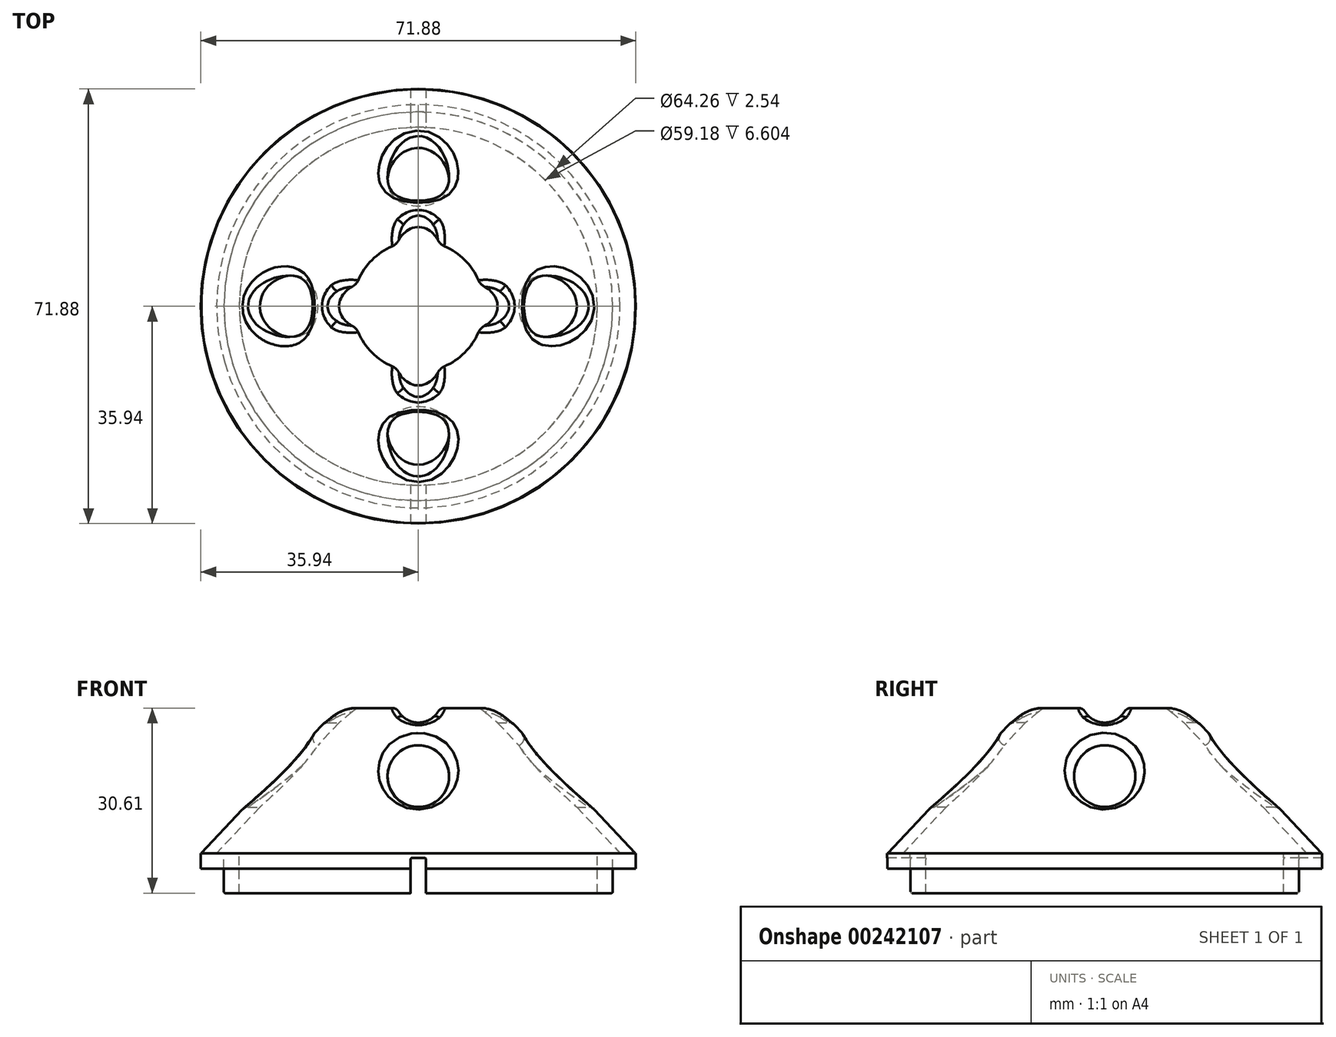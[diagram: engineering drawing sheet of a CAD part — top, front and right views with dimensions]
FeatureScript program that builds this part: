
annotation { "Feature Type Name" : "Feature", "Feature Type Description" : "" }
export const myFeature = defineFeature(function(context is Context, id is Id, definition is map)
    precondition{}
    {
        {
            var Q0;
            Q0=qCreatedBy(makeId("Top.planeOp"),FACE);
            var sketch = newSketch(context, id + "F0", { "sketchPlane" : qUnion([Q0])});
            skCircle(sketch, "E0", {"center": v(0, 0) * mm, "radius": 32.13 * mm});
            skCircle(sketch, "E1", {"center": v(0, 0) * mm, "radius": 35.94 * mm});
            skCircle(sketch, "E2", {"center": v(0, 0) * mm, "radius": 29.6 * mm});
            skSolve(sketch);
        }
        {
            var Q0;
            Q0=makeQuery(id+"F0.imprint","IMPRINT",FACE,{"disambiguationData":[TD([[makeQuery(id+"F0.imprint","IMPRINT",EDGE,{"derivedFrom":sQuery(id+"F0.wireOp",EDGE,"E0")}),1.0]])]});
            extrude(context, id + "F1", {"entities" : qUnion([Q0]), "oppositeDirection" : true, "depth" : 6.6 * mm});
        }
        {
            var Q0;
            Q0=makeQuery(id+"F0.imprint","IMPRINT",FACE,{"disambiguationData":[TD([[makeQuery(id+"F0.imprint","IMPRINT",EDGE,{"derivedFrom":sQuery(id+"F0.wireOp",EDGE,"E0")}),-1.0]])]});
            extrude(context, id + "F2", {"entities" : qUnion([Q0]), "oppositeDirection" : true, "depth" : 2.54 * mm});
        }
        {
            var Q0;
            Q0=qCreatedBy(makeId("Front.planeOp"),FACE);
            var sketch = newSketch(context, id + "F3", { "sketchPlane" : qUnion([Q0])});
            skPoint(sketch, "E3", {"position": v(-35.87, 0) * mm});
            skPoint(sketch, "E4", {"position": v(-33.33, 0) * mm});
            skPoint(sketch, "E5", {"position": v(0, 38.1) * mm});
            skPoint(sketch, "E6", {"position": v(0, 35.56) * mm});
            skLineSegment(sketch, "E7", {"start": v(0, 38.1) * mm, "end": v(-35.87, 0) * mm});
            skLineSegment(sketch, "E8", {"start": v(0, 35.56) * mm, "end": v(-33.33, 0) * mm});
            skLineSegment(sketch, "E9", {"start": v(0, 38.1) * mm, "end": v(0, 35.56) * mm});
            skLineSegment(sketch, "E10", {"start": v(-35.87, 0) * mm, "end": v(-33.33, 0) * mm});
            skSolve(sketch);
        }
        {
            var Q0;
            Q0=makeQuery(id+"F3.imprint","IMPRINT",FACE,{"disambiguationData":[TD([[makeQuery(id+"F3.imprint","IMPRINT",EDGE,{"derivedFrom":sQuery(id+"F3.wireOp",EDGE,"E7")}),1.0]])]});
            var Q1;
            Q1=sQuery(id+"F3.wireOp",EDGE,"E9");
            revolve(context, id + "F4", {"entities" : qUnion([Q0]), "axis" : qUnion([Q1]), "revolveType" : RevolveType.FULL});
        }
        {
            var Q0;
            Q0=qCreatedBy(makeId("Front.planeOp"),FACE);
            var sketch = newSketch(context, id + "F5", { "sketchPlane" : qUnion([Q0])});
            skPoint(sketch, "E11", {"position": v(0, 25.4) * mm});
            skCircle(sketch, "E12", {"center": v(0, 25.4) * mm, "radius": 3.81 * mm});
            skPoint(sketch, "E13", {"position": v(0, 12.7) * mm});
            skCircle(sketch, "E14", {"center": v(0, 12.7) * mm, "radius": 5.08 * mm});
            skSolve(sketch);
        }
        {
            var Q0;
            Q0 = qSketchRegion(id + "F5", true);
            extrude(context, id + "F6", {"entities" : qUnion([Q0]), "operationType" : NewBodyOperationType.REMOVE, "endBound" : BoundingType.SYMMETRIC, "oppositeDirection" : true, "depth" : 76.2 * mm});
        }
        {
            var Q0;
            Q0=qCreatedBy(makeId("Right.planeOp"),FACE);
            var sketch = newSketch(context, id + "F7", { "sketchPlane" : qUnion([Q0])});
            skPoint(sketch, "E15", {"position": v(0, 25.4) * mm});
            skCircle(sketch, "E16", {"center": v(0, 25.4) * mm, "radius": 3.81 * mm});
            skCircle(sketch, "E17", {"center": v(0, 12.7) * mm, "radius": 5.08 * mm});
            skSolve(sketch);
        }
        {
            var Q0;
            Q0 = qSketchRegion(id + "F7", true);
            extrude(context, id + "F8", {"entities" : qUnion([Q0]), "operationType" : NewBodyOperationType.REMOVE, "endBound" : BoundingType.SYMMETRIC, "oppositeDirection" : true, "depth" : 76.2 * mm});
        }
        {
            var Q0;
            Q0=qCreatedBy(makeId("Front.planeOp"),FACE);
            var sketch = newSketch(context, id + "F9", { "sketchPlane" : qUnion([Q0])});
            skLineSegment(sketch, "E18.bottom", {"start": v(1.27, -0.77) * mm, "end": v(-1.27, -0.77) * mm});
            skLineSegment(sketch, "E18.top", {"start": v(1.27, -14.3) * mm, "end": v(-1.27, -14.3) * mm});
            skLineSegment(sketch, "E18.left", {"start": v(1.27, -0.77) * mm, "end": v(1.27, -14.3) * mm});
            skLineSegment(sketch, "E18.right", {"start": v(-1.27, -0.77) * mm, "end": v(-1.27, -14.3) * mm});
            skPoint(sketch, "E18.middle", {"position": v(0, -7.54) * mm});
            skSolve(sketch);
        }
        {
            var Q0;
            Q0 = qSketchRegion(id + "F9", true);
            extrude(context, id + "F10", {"entities" : qUnion([Q0]), "operationType" : NewBodyOperationType.REMOVE, "endBound" : BoundingType.SYMMETRIC, "oppositeDirection" : true, "depth" : 127 * mm});
        }
        {
            var Q0;
            {var subQ0=sQuery(id+"F9.wireOp",EDGE,"E18.bottom");var subQ1=sQuery(id+"F9.wireOp",EDGE,"E18.left");Q0=makeQuery(id+"F10.boolean.opBoolean","COPY",EDGE,{"disambiguationData":[TD([makeQuery(id+"F2.opExtrude","SWEPT_FACE",FACE,{"disambiguationData":[OSD([sQuery(id+"F0.wireOp",EDGE,"E0")])]}),makeQuery(id+"F2.opExtrude","SWEPT_FACE",FACE,{"disambiguationData":[OSD([sQuery(id+"F0.wireOp",EDGE,"E1")])]}),makeQuery(id+"F10.opExtrude","SWEPT_FACE",FACE,{"disambiguationData":[OSD([subQ0])]}),makeQuery(id+"F10.opExtrude","SWEPT_FACE",FACE,{"disambiguationData":[OSD([subQ1])]})]),OD(0.0)],"derivedFrom":makeQuery(id+"F10.opExtrude","SWEPT_EDGE",EDGE,{"disambiguationData":[OSD([subQ0,subQ1])]})});}
            var Q1;
            {var subQ0=sQuery(id+"F9.wireOp",EDGE,"E18.left");var subQ1=sQuery(id+"F9.wireOp",EDGE,"E18.bottom");Q1=makeQuery(id+"F10.boolean.opBoolean","COPY",EDGE,{"disambiguationData":[TD([makeQuery(id+"F1.opExtrude","SWEPT_FACE",FACE,{"disambiguationData":[OSD([sQuery(id+"F0.wireOp",EDGE,"E0")])]}),makeQuery(id+"F1.opExtrude","SWEPT_FACE",FACE,{"disambiguationData":[OSD([sQuery(id+"F0.wireOp",EDGE,"E2")])]}),makeQuery(id+"F10.opExtrude","SWEPT_FACE",FACE,{"disambiguationData":[OSD([subQ1])]}),makeQuery(id+"F10.opExtrude","SWEPT_FACE",FACE,{"disambiguationData":[OSD([subQ0])]})]),OD(0.0)],"derivedFrom":makeQuery(id+"F10.opExtrude","SWEPT_EDGE",EDGE,{"disambiguationData":[OSD([subQ1,subQ0])]})});}
            var Q2;
            {var subQ0=sQuery(id+"F9.wireOp",EDGE,"E18.bottom");var subQ1=sQuery(id+"F9.wireOp",EDGE,"E18.right");Q2=makeQuery(id+"F10.boolean.opBoolean","COPY",EDGE,{"disambiguationData":[TD([makeQuery(id+"F1.opExtrude","SWEPT_FACE",FACE,{"disambiguationData":[OSD([sQuery(id+"F0.wireOp",EDGE,"E0")])]}),makeQuery(id+"F1.opExtrude","SWEPT_FACE",FACE,{"disambiguationData":[OSD([sQuery(id+"F0.wireOp",EDGE,"E2")])]}),makeQuery(id+"F10.opExtrude","SWEPT_FACE",FACE,{"disambiguationData":[OSD([subQ0])]}),makeQuery(id+"F10.opExtrude","SWEPT_FACE",FACE,{"disambiguationData":[OSD([subQ1])]})]),OD(0.0)],"derivedFrom":makeQuery(id+"F10.opExtrude","SWEPT_EDGE",EDGE,{"disambiguationData":[OSD([subQ0,subQ1])]})});}
            var Q3;
            {var subQ0=sQuery(id+"F9.wireOp",EDGE,"E18.bottom");var subQ1=sQuery(id+"F9.wireOp",EDGE,"E18.right");Q3=makeQuery(id+"F10.boolean.opBoolean","COPY",EDGE,{"disambiguationData":[TD([makeQuery(id+"F2.opExtrude","SWEPT_FACE",FACE,{"disambiguationData":[OSD([sQuery(id+"F0.wireOp",EDGE,"E0")])]}),makeQuery(id+"F2.opExtrude","SWEPT_FACE",FACE,{"disambiguationData":[OSD([sQuery(id+"F0.wireOp",EDGE,"E1")])]}),makeQuery(id+"F10.opExtrude","SWEPT_FACE",FACE,{"disambiguationData":[OSD([subQ0])]}),makeQuery(id+"F10.opExtrude","SWEPT_FACE",FACE,{"disambiguationData":[OSD([subQ1])]})]),OD(0.0)],"derivedFrom":makeQuery(id+"F10.opExtrude","SWEPT_EDGE",EDGE,{"disambiguationData":[OSD([subQ0,subQ1])]})});}
            var Q4;
            {var subQ0=sQuery(id+"F9.wireOp",EDGE,"E18.bottom");var subQ1=sQuery(id+"F9.wireOp",EDGE,"E18.right");Q4=makeQuery(id+"F10.boolean.opBoolean","COPY",EDGE,{"disambiguationData":[TD([makeQuery(id+"F2.opExtrude","SWEPT_FACE",FACE,{"disambiguationData":[OSD([sQuery(id+"F0.wireOp",EDGE,"E0")])]}),makeQuery(id+"F2.opExtrude","SWEPT_FACE",FACE,{"disambiguationData":[OSD([sQuery(id+"F0.wireOp",EDGE,"E1")])]}),makeQuery(id+"F10.opExtrude","SWEPT_FACE",FACE,{"disambiguationData":[OSD([subQ0])]}),makeQuery(id+"F10.opExtrude","SWEPT_FACE",FACE,{"disambiguationData":[OSD([subQ1])]})]),OD(1.0)],"derivedFrom":makeQuery(id+"F10.opExtrude","SWEPT_EDGE",EDGE,{"disambiguationData":[OSD([subQ0,subQ1])]})});}
            var Q5;
            {var subQ0=sQuery(id+"F9.wireOp",EDGE,"E18.bottom");var subQ1=sQuery(id+"F9.wireOp",EDGE,"E18.right");Q5=makeQuery(id+"F10.boolean.opBoolean","COPY",EDGE,{"disambiguationData":[TD([makeQuery(id+"F1.opExtrude","SWEPT_FACE",FACE,{"disambiguationData":[OSD([sQuery(id+"F0.wireOp",EDGE,"E0")])]}),makeQuery(id+"F1.opExtrude","SWEPT_FACE",FACE,{"disambiguationData":[OSD([sQuery(id+"F0.wireOp",EDGE,"E2")])]}),makeQuery(id+"F10.opExtrude","SWEPT_FACE",FACE,{"disambiguationData":[OSD([subQ0])]}),makeQuery(id+"F10.opExtrude","SWEPT_FACE",FACE,{"disambiguationData":[OSD([subQ1])]})]),OD(1.0)],"derivedFrom":makeQuery(id+"F10.opExtrude","SWEPT_EDGE",EDGE,{"disambiguationData":[OSD([subQ0,subQ1])]})});}
            var Q6;
            {var subQ0=sQuery(id+"F9.wireOp",EDGE,"E18.bottom");var subQ1=sQuery(id+"F9.wireOp",EDGE,"E18.left");Q6=makeQuery(id+"F10.boolean.opBoolean","COPY",EDGE,{"disambiguationData":[TD([makeQuery(id+"F2.opExtrude","SWEPT_FACE",FACE,{"disambiguationData":[OSD([sQuery(id+"F0.wireOp",EDGE,"E0")])]}),makeQuery(id+"F2.opExtrude","SWEPT_FACE",FACE,{"disambiguationData":[OSD([sQuery(id+"F0.wireOp",EDGE,"E1")])]}),makeQuery(id+"F10.opExtrude","SWEPT_FACE",FACE,{"disambiguationData":[OSD([subQ0])]}),makeQuery(id+"F10.opExtrude","SWEPT_FACE",FACE,{"disambiguationData":[OSD([subQ1])]})]),OD(1.0)],"derivedFrom":makeQuery(id+"F10.opExtrude","SWEPT_EDGE",EDGE,{"disambiguationData":[OSD([subQ0,subQ1])]})});}
            var Q7;
            {var subQ0=sQuery(id+"F9.wireOp",EDGE,"E18.left");var subQ1=sQuery(id+"F9.wireOp",EDGE,"E18.bottom");Q7=makeQuery(id+"F10.boolean.opBoolean","COPY",EDGE,{"disambiguationData":[TD([makeQuery(id+"F1.opExtrude","SWEPT_FACE",FACE,{"disambiguationData":[OSD([sQuery(id+"F0.wireOp",EDGE,"E0")])]}),makeQuery(id+"F1.opExtrude","SWEPT_FACE",FACE,{"disambiguationData":[OSD([sQuery(id+"F0.wireOp",EDGE,"E2")])]}),makeQuery(id+"F10.opExtrude","SWEPT_FACE",FACE,{"disambiguationData":[OSD([subQ1])]}),makeQuery(id+"F10.opExtrude","SWEPT_FACE",FACE,{"disambiguationData":[OSD([subQ0])]})]),OD(1.0)],"derivedFrom":makeQuery(id+"F10.opExtrude","SWEPT_EDGE",EDGE,{"disambiguationData":[OSD([subQ1,subQ0])]})});}
            var Q8;
            {var subQ0=sQuery(id+"F0.wireOp",EDGE,"E0");Q8=makeQuery(id+"F10.boolean.opBoolean","SPLIT",EDGE,{"disambiguationData":[TD([makeQuery(id+"F10.opExtrude","SWEPT_FACE",FACE,{"disambiguationData":[OSD([sQuery(id+"F9.wireOp",EDGE,"E18.right")])]})])],"derivedFrom":makeQuery(id+"F1.opExtrude","CAP_EDGE",EDGE,{"disambiguationData":[OSD([subQ0])],"isStart":false})});}
            var Q9;
            {var subQ0=sQuery(id+"F0.wireOp",EDGE,"E0");Q9=makeQuery(id+"F10.boolean.opBoolean","SPLIT",EDGE,{"disambiguationData":[TD([makeQuery(id+"F10.opExtrude","SWEPT_FACE",FACE,{"disambiguationData":[OSD([sQuery(id+"F9.wireOp",EDGE,"E18.left")])]})])],"derivedFrom":makeQuery(id+"F1.opExtrude","CAP_EDGE",EDGE,{"disambiguationData":[OSD([subQ0])],"isStart":false})});}
            fillet(context, id + "F11", {"entities" : qUnion([Q0, Q1, Q2, Q3, Q4, Q5, Q6, Q7, Q8, Q9]), "radius" : 0.25 * mm, "tangentPropagation" : true, "allowEdgeOverflow" : false});
        }
        {
            var Q0;
            Q0=qCreatedBy(makeId("Top.planeOp"),FACE);
            var sketch = newSketch(context, id + "F12", { "sketchPlane" : qUnion([Q0])});
            skCircle(sketch, "E19", {"center": v(0, 0) * mm, "radius": 10.83 * mm});
            skSolve(sketch);
        }
        {
            var Q0;
            Q0 = qSketchRegion(id + "F12", true);
            extrude(context, id + "F13", {"entities" : qUnion([Q0]), "operationType" : NewBodyOperationType.REMOVE, "depth" : 50.8 * mm});
        }
        {
            var Q0;
            Q0=makeQuery(id+"F13.boolean.opBoolean","INTERSECT",EDGE,{"disambiguationData":[OD(2.0)],"derivedFrom":[makeQuery(id+"F4.opRevolve","SWEPT_FACE",FACE,{"disambiguationData":[OSD([sQuery(id+"F3.wireOp",EDGE,"E7")])]}),makeQuery(id+"F13.opExtrude","SWEPT_FACE",FACE,{"disambiguationData":[OSD([sQuery(id+"F12.wireOp",EDGE,"E19")])]})]});
            var Q1;
            Q1=makeQuery(id+"F13.boolean.opBoolean","INTERSECT",EDGE,{"disambiguationData":[OD(1.0)],"derivedFrom":[makeQuery(id+"F4.opRevolve","SWEPT_FACE",FACE,{"disambiguationData":[OSD([sQuery(id+"F3.wireOp",EDGE,"E7")])]}),makeQuery(id+"F13.opExtrude","SWEPT_FACE",FACE,{"disambiguationData":[OSD([sQuery(id+"F12.wireOp",EDGE,"E19")])]})]});
            var Q2;
            Q2=makeQuery(id+"F13.boolean.opBoolean","INTERSECT",EDGE,{"disambiguationData":[OD(0.0)],"derivedFrom":[makeQuery(id+"F4.opRevolve","SWEPT_FACE",FACE,{"disambiguationData":[OSD([sQuery(id+"F3.wireOp",EDGE,"E7")])]}),makeQuery(id+"F13.opExtrude","SWEPT_FACE",FACE,{"disambiguationData":[OSD([sQuery(id+"F12.wireOp",EDGE,"E19")])]})]});
            var Q3;
            Q3=makeQuery(id+"F13.boolean.opBoolean","INTERSECT",EDGE,{"disambiguationData":[OD(3.0)],"derivedFrom":[makeQuery(id+"F4.opRevolve","SWEPT_FACE",FACE,{"disambiguationData":[OSD([sQuery(id+"F3.wireOp",EDGE,"E7")])]}),makeQuery(id+"F13.opExtrude","SWEPT_FACE",FACE,{"disambiguationData":[OSD([sQuery(id+"F12.wireOp",EDGE,"E19")])]})]});
            fillet(context, id + "F14", {"entities" : qUnion([Q0, Q1, Q2, Q3]), "radius" : 5.08 * mm, "tangentPropagation" : true, "allowEdgeOverflow" : false});
        }
        {
            var Q0;
            Q0=makeQuery(id+"F8.boolean.opBoolean","INTERSECT",EDGE,{"disambiguationData":[OD(0.0)],"derivedFrom":[makeQuery(id+"F4.opRevolve","SWEPT_FACE",FACE,{"disambiguationData":[OSD([sQuery(id+"F3.wireOp",EDGE,"E7")])]}),makeQuery(id+"F8.opExtrude","SWEPT_FACE",FACE,{"disambiguationData":[OSD([sQuery(id+"F7.wireOp",EDGE,"E17")])]})]});
            var Q1;
            Q1=makeQuery(id+"F8.boolean.opBoolean","INTERSECT",EDGE,{"disambiguationData":[OD(1.0)],"derivedFrom":[makeQuery(id+"F4.opRevolve","SWEPT_FACE",FACE,{"disambiguationData":[OSD([sQuery(id+"F3.wireOp",EDGE,"E7")])]}),makeQuery(id+"F8.opExtrude","SWEPT_FACE",FACE,{"disambiguationData":[OSD([sQuery(id+"F7.wireOp",EDGE,"E17")])]})]});
            var Q2;
            Q2=makeQuery(id+"F6.boolean.opBoolean","INTERSECT",EDGE,{"disambiguationData":[OD(1.0)],"derivedFrom":[makeQuery(id+"F4.opRevolve","SWEPT_FACE",FACE,{"disambiguationData":[OSD([sQuery(id+"F3.wireOp",EDGE,"E7")])]}),makeQuery(id+"F6.opExtrude","SWEPT_FACE",FACE,{"disambiguationData":[OSD([sQuery(id+"F5.wireOp",EDGE,"E14")])]})]});
            var Q3;
            Q3=makeQuery(id+"F6.boolean.opBoolean","INTERSECT",EDGE,{"disambiguationData":[OD(0.0)],"derivedFrom":[makeQuery(id+"F4.opRevolve","SWEPT_FACE",FACE,{"disambiguationData":[OSD([sQuery(id+"F3.wireOp",EDGE,"E7")])]}),makeQuery(id+"F6.opExtrude","SWEPT_FACE",FACE,{"disambiguationData":[OSD([sQuery(id+"F5.wireOp",EDGE,"E14")])]})]});
            var Q4;
            Q4=makeQuery(id+"F8.boolean.opBoolean","INTERSECT",EDGE,{"disambiguationData":[OD(1.0)],"derivedFrom":[makeQuery(id+"F4.opRevolve","SWEPT_FACE",FACE,{"disambiguationData":[OSD([sQuery(id+"F3.wireOp",EDGE,"E7")])]}),makeQuery(id+"F8.opExtrude","SWEPT_FACE",FACE,{"disambiguationData":[OSD([sQuery(id+"F7.wireOp",EDGE,"E16")])]})]});
            var Q5;
            Q5=makeQuery(id+"F6.boolean.opBoolean","INTERSECT",EDGE,{"disambiguationData":[OD(1.0)],"derivedFrom":[makeQuery(id+"F4.opRevolve","SWEPT_FACE",FACE,{"disambiguationData":[OSD([sQuery(id+"F3.wireOp",EDGE,"E7")])]}),makeQuery(id+"F6.opExtrude","SWEPT_FACE",FACE,{"disambiguationData":[OSD([sQuery(id+"F5.wireOp",EDGE,"E12")])]})]});
            var Q6;
            Q6=makeQuery(id+"F8.boolean.opBoolean","INTERSECT",EDGE,{"disambiguationData":[OD(0.0)],"derivedFrom":[makeQuery(id+"F4.opRevolve","SWEPT_FACE",FACE,{"disambiguationData":[OSD([sQuery(id+"F3.wireOp",EDGE,"E7")])]}),makeQuery(id+"F8.opExtrude","SWEPT_FACE",FACE,{"disambiguationData":[OSD([sQuery(id+"F7.wireOp",EDGE,"E16")])]})]});
            var Q7;
            Q7=makeQuery(id+"F6.boolean.opBoolean","INTERSECT",EDGE,{"disambiguationData":[OD(0.0)],"derivedFrom":[makeQuery(id+"F4.opRevolve","SWEPT_FACE",FACE,{"disambiguationData":[OSD([sQuery(id+"F3.wireOp",EDGE,"E7")])]}),makeQuery(id+"F6.opExtrude","SWEPT_FACE",FACE,{"disambiguationData":[OSD([sQuery(id+"F5.wireOp",EDGE,"E12")])]})]});
            fillet(context, id + "F15", {"entities" : qUnion([Q0, Q1, Q2, Q3, Q4, Q5, Q6, Q7]), "radius" : 1.27 * mm, "tangentPropagation" : true, "allowEdgeOverflow" : false});
        }
    });
